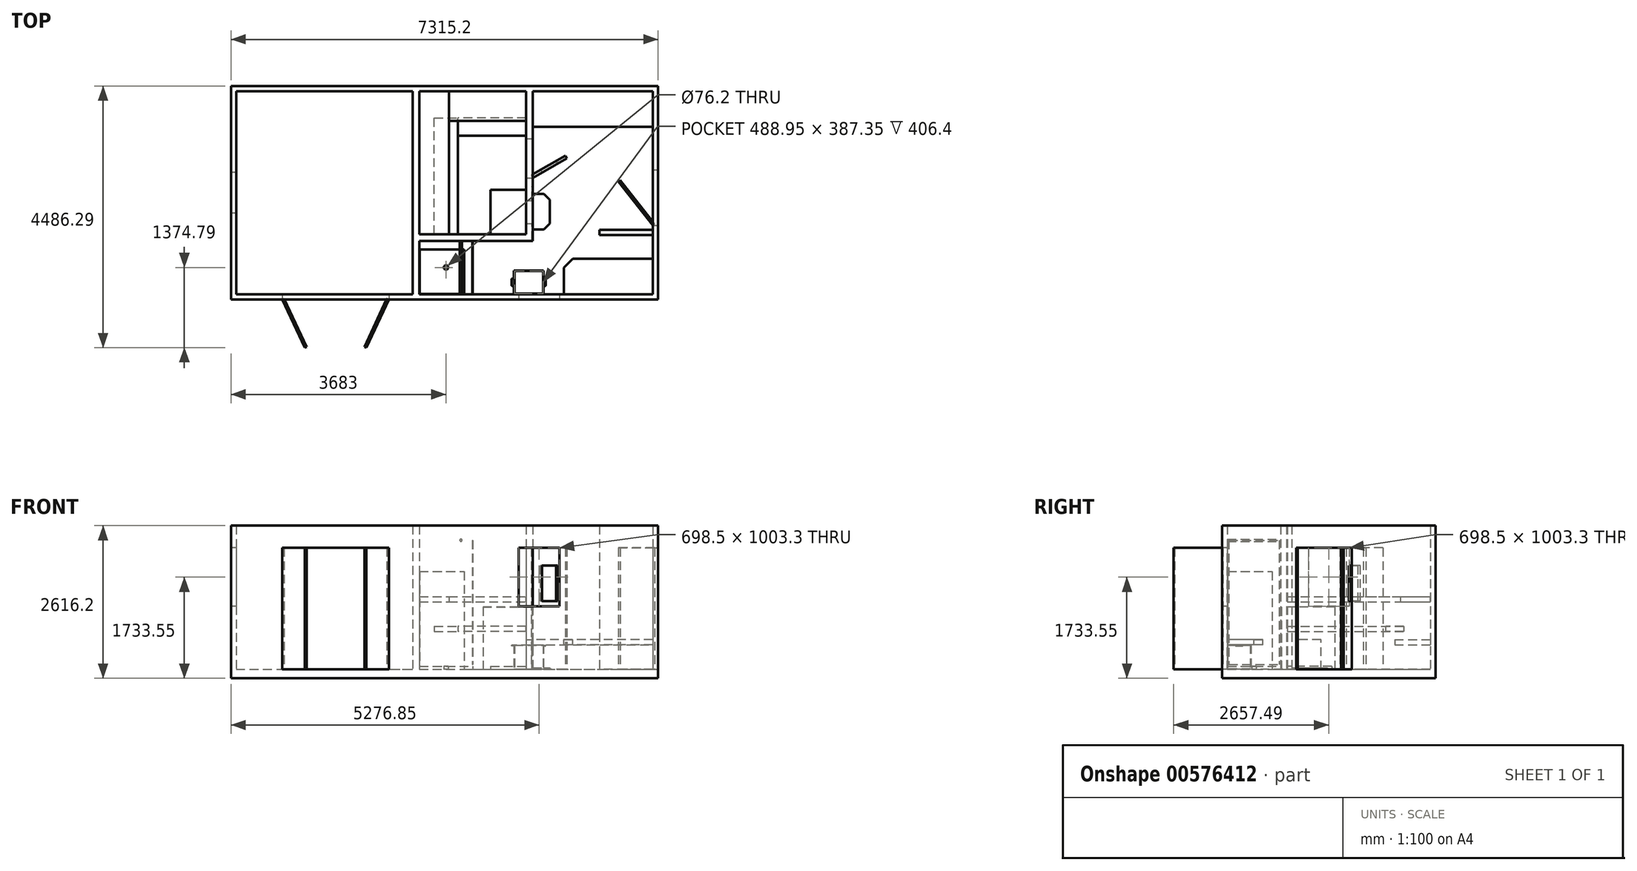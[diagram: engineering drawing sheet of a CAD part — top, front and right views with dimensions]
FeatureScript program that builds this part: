
annotation { "Feature Type Name" : "Feature", "Feature Type Description" : "" }
export const myFeature = defineFeature(function(context is Context, id is Id, definition is map)
    precondition{}
    {
        {
            var Q0;
            Q0=qCreatedBy(makeId("Top.planeOp"),FACE);
            var sketch = newSketch(context, id + "F0", { "sketchPlane" : qUnion([Q0])});
            skLineSegment(sketch, "E0.bottom", {"start": v(-3657.6, -1828.8) * mm, "end": v(3657.6, -1828.8) * mm});
            skLineSegment(sketch, "E0.top", {"start": v(-3657.6, 1828.8) * mm, "end": v(3657.6, 1828.8) * mm});
            skLineSegment(sketch, "E0.left", {"start": v(-3657.6, -1828.8) * mm, "end": v(-3657.6, 1828.8) * mm});
            skLineSegment(sketch, "E0.right", {"start": v(3657.6, -1828.8) * mm, "end": v(3657.6, 1828.8) * mm});
            skPoint(sketch, "E0.middle", {"position": v(0, 0) * mm});
            skSolve(sketch);
        }
        {
            var Q0;
            Q0=makeQuery(id+"F0.imprint","IMPRINT",FACE,{"disambiguationData":[TD([[makeQuery(id+"F0.imprint","IMPRINT",EDGE,{"derivedFrom":sQuery(id+"F0.wireOp",EDGE,"E0.bottom")}),1.0]])]});
            extrude(context, id + "F1", {"entities" : qUnion([Q0]), "depth" : 152.4 * mm});
        }
        {
            var Q0;
            Q0=makeQuery(id+"F1.opExtrude","CAP_FACE",FACE,{"disambiguationData":[OSD([sQuery(id+"F0.wireOp",EDGE,"E0.bottom"),sQuery(id+"F0.wireOp",EDGE,"E0.top"),sQuery(id+"F0.wireOp",EDGE,"E0.left"),sQuery(id+"F0.wireOp",EDGE,"E0.right")])],"isStart":false});
            var sketch = newSketch(context, id + "F2", { "sketchPlane" : qUnion([Q0])});
            skLineSegment(sketch, "E1.0", {"start": v(-3657.6, -1828.8) * mm, "end": v(-3657.6, 1828.8) * mm});
            skLineSegment(sketch, "E1.1", {"start": v(-3657.6, 1828.8) * mm, "end": v(3657.6, 1828.8) * mm});
            skLineSegment(sketch, "E1.2", {"start": v(3657.6, -1828.8) * mm, "end": v(3657.6, 1828.8) * mm});
            skLineSegment(sketch, "E1.3", {"start": v(-3657.6, -1828.8) * mm, "end": v(3657.6, -1828.8) * mm});
            skLineSegment(sketch, "E2.bottom", {"start": v(-3568.7, 1739.9) * mm, "end": v(3568.7, 1739.9) * mm});
            skLineSegment(sketch, "E2.top", {"start": v(-3568.7, -1739.9) * mm, "end": v(3568.7, -1739.9) * mm});
            skLineSegment(sketch, "E2.left", {"start": v(-3568.7, 1739.9) * mm, "end": v(-3568.7, -1739.9) * mm});
            skLineSegment(sketch, "E2.right", {"start": v(3568.7, 1739.9) * mm, "end": v(3568.7, -1739.9) * mm});
            skLineSegment(sketch, "E3", {"start": v(3568.7, 0) * mm, "end": v(0, 0) * mm, "construction": true});
            skSolve(sketch);
        }
        {
            var Q0;
            Q0=qSketchRegion(id+"F2",true);
            extrude(context, id + "F3", {"entities" : qUnion([Q0]), "depth" : 2463.8 * mm});
        }
        {
            var Q0;
            Q0=makeQuery(id+"F3.opExtrude","SWEPT_FACE",FACE,{"disambiguationData":[OSD([sQuery(id+"F2.wireOp",EDGE,"E1.2")])]});
            var sketch = newSketch(context, id + "F4", { "sketchPlane" : qUnion([Q0])});
            skLineSegment(sketch, "E4.bottom", {"start": v(-558.8, 152.4) * mm, "end": v(393.7, 152.4) * mm});
            skLineSegment(sketch, "E4.top", {"start": v(-558.8, 2235.2) * mm, "end": v(393.7, 2235.2) * mm});
            skLineSegment(sketch, "E4.left", {"start": v(-558.8, 152.4) * mm, "end": v(-558.8, 2235.2) * mm});
            skLineSegment(sketch, "E4.right", {"start": v(393.7, 152.4) * mm, "end": v(393.7, 2235.2) * mm});
            skSolve(sketch);
        }
        {
            var Q0;
            Q0=qSketchRegion(id+"F4",true);
            extrude(context, id + "F5", {"entities" : qUnion([Q0]), "operationType" : NewBodyOperationType.REMOVE, "endBound" : BoundingType.UP_TO_NEXT, "oppositeDirection" : true, "depth" : 25.4 * mm});
        }
        {
            var Q0;
            Q0=makeQuery(id+"F3.opExtrude","SWEPT_FACE",FACE,{"disambiguationData":[OSD([sQuery(id+"F2.wireOp",EDGE,"E1.3")])]});
            var sketch = newSketch(context, id + "F6", { "sketchPlane" : qUnion([Q0])});
            skLineSegment(sketch, "E5.bottom", {"start": v(-2781.3, 152.4) * mm, "end": v(-952.5, 152.4) * mm});
            skLineSegment(sketch, "E5.top", {"start": v(-2781.3, 2235.2) * mm, "end": v(-952.5, 2235.2) * mm});
            skLineSegment(sketch, "E5.left", {"start": v(-2781.3, 152.4) * mm, "end": v(-2781.3, 2235.2) * mm});
            skLineSegment(sketch, "E5.right", {"start": v(-952.5, 152.4) * mm, "end": v(-952.5, 2235.2) * mm});
            skLineSegment(sketch, "E6.bottom", {"start": v(1270, 2235.2) * mm, "end": v(1968.5, 2235.2) * mm});
            skLineSegment(sketch, "E6.top", {"start": v(1270, 1231.9) * mm, "end": v(1968.5, 1231.9) * mm});
            skLineSegment(sketch, "E6.left", {"start": v(1270, 2235.2) * mm, "end": v(1270, 1231.9) * mm});
            skLineSegment(sketch, "E6.right", {"start": v(1968.5, 2235.2) * mm, "end": v(1968.5, 1231.9) * mm});
            skSolve(sketch);
        }
        {
            var Q0;
            Q0=qSketchRegion(id+"F6",true);
            extrude(context, id + "F7", {"entities" : qUnion([Q0]), "operationType" : NewBodyOperationType.REMOVE, "endBound" : BoundingType.UP_TO_NEXT, "oppositeDirection" : true, "depth" : 25.4 * mm});
        }
        {
            var Q0;
            Q0=makeQuery(id+"F3.opExtrude","SWEPT_FACE",FACE,{"disambiguationData":[OSD([sQuery(id+"F2.wireOp",EDGE,"E1.0")])]});
            var sketch = newSketch(context, id + "F8", { "sketchPlane" : qUnion([Q0])});
            skLineSegment(sketch, "E7.bottom", {"start": v(-349.25, 2235.2) * mm, "end": v(349.25, 2235.2) * mm});
            skLineSegment(sketch, "E7.top", {"start": v(-349.25, 1231.9) * mm, "end": v(349.25, 1231.9) * mm});
            skLineSegment(sketch, "E7.left", {"start": v(-349.25, 2235.2) * mm, "end": v(-349.25, 1231.9) * mm});
            skLineSegment(sketch, "E7.right", {"start": v(349.25, 2235.2) * mm, "end": v(349.25, 1231.9) * mm});
            skLineSegment(sketch, "E8", {"start": v(0, 2235.2) * mm, "end": v(0, 1231.9) * mm, "construction": true});
            skSolve(sketch);
        }
        {
            var Q0;
            Q0=qSketchRegion(id+"F8",true);
            extrude(context, id + "F9", {"entities" : qUnion([Q0]), "operationType" : NewBodyOperationType.REMOVE, "endBound" : BoundingType.UP_TO_NEXT, "oppositeDirection" : true, "depth" : 25.4 * mm});
        }
        {
            var Q0;
            Q0=makeQuery(id+"F1.opExtrude","CAP_FACE",FACE,{"disambiguationData":[OSD([sQuery(id+"F0.wireOp",EDGE,"E0.bottom"),sQuery(id+"F0.wireOp",EDGE,"E0.top"),sQuery(id+"F0.wireOp",EDGE,"E0.left"),sQuery(id+"F0.wireOp",EDGE,"E0.right")])],"isStart":false});
            var sketch = newSketch(context, id + "F10", { "sketchPlane" : qUnion([Q0])});
            skLineSegment(sketch, "E9.bottom", {"start": v(-546.1, -1739.9) * mm, "end": v(-431.8, -1739.9) * mm});
            skLineSegment(sketch, "E9.top", {"start": v(-546.1, 1739.9) * mm, "end": v(-431.8, 1739.9) * mm});
            skLineSegment(sketch, "E9.left", {"start": v(-546.1, -1739.9) * mm, "end": v(-546.1, 1739.9) * mm});
            skLineSegment(sketch, "E9.right", {"start": v(-431.8, -1739.9) * mm, "end": v(-431.8, 1739.9) * mm});
            skLineSegment(sketch, "E10.top", {"start": v(1397, 1739.9) * mm, "end": v(1511.3, 1739.9) * mm});
            skLineSegment(sketch, "E11", {"start": v(1397, 1739.9) * mm, "end": v(1397, -711.2) * mm});
            skLineSegment(sketch, "E12", {"start": v(1397, -711.2) * mm, "end": v(-431.8, -711.2) * mm});
            skLineSegment(sketch, "E13", {"start": v(-431.8, -711.2) * mm, "end": v(-431.8, -825.5) * mm});
            skLineSegment(sketch, "E14", {"start": v(-431.8, -825.5) * mm, "end": v(1511.3, -825.5) * mm});
            skLineSegment(sketch, "E15", {"start": v(1511.3, -825.5) * mm, "end": v(1511.3, 1739.9) * mm});
            skSolve(sketch);
        }
        {
            var Q0;
            Q0=qSketchRegion(id+"F10",true);
            var Q1;
            Q1=makeQuery(id+"F3.opExtrude","CAP_FACE",FACE,{"disambiguationData":[OSD([sQuery(id+"F2.wireOp",EDGE,"E1.0"),sQuery(id+"F2.wireOp",EDGE,"E1.1"),sQuery(id+"F2.wireOp",EDGE,"E1.2"),sQuery(id+"F2.wireOp",EDGE,"E1.3"),sQuery(id+"F2.wireOp",EDGE,"E2.bottom"),sQuery(id+"F2.wireOp",EDGE,"E2.top"),sQuery(id+"F2.wireOp",EDGE,"E2.left"),sQuery(id+"F2.wireOp",EDGE,"E2.right")])],"isStart":false});
            extrude(context, id + "F11", {"entities" : qUnion([Q0]), "endBound" : BoundingType.UP_TO_SURFACE, "endBoundEntityFace" : qUnion([Q1]), "depth" : 25.4 * mm});
        }
        {
            var Q0;
            Q0=makeQuery(id+"F1.opExtrude","CAP_FACE",FACE,{"disambiguationData":[OSD([sQuery(id+"F0.wireOp",EDGE,"E0.bottom"),sQuery(id+"F0.wireOp",EDGE,"E0.top"),sQuery(id+"F0.wireOp",EDGE,"E0.left"),sQuery(id+"F0.wireOp",EDGE,"E0.right")])],"isStart":false});
            var sketch = newSketch(context, id + "F12", { "sketchPlane" : qUnion([Q0])});
            skLineSegment(sketch, "E16.bottom", {"start": v(3568.7, -723.9) * mm, "end": v(2654.3, -723.9) * mm});
            skLineSegment(sketch, "E16.top", {"start": v(3568.7, -635) * mm, "end": v(2654.3, -635) * mm});
            skLineSegment(sketch, "E16.left", {"start": v(3568.7, -723.9) * mm, "end": v(3568.7, -635) * mm});
            skLineSegment(sketch, "E16.right", {"start": v(2654.3, -723.9) * mm, "end": v(2654.3, -635) * mm});
            skSolve(sketch);
        }
        {
            var Q0;
            Q0=qSketchRegion(id+"F12",true);
            var Q1;
            Q1=makeQuery(id+"F3.opExtrude","CAP_FACE",FACE,{"disambiguationData":[OSD([sQuery(id+"F2.wireOp",EDGE,"E1.0"),sQuery(id+"F2.wireOp",EDGE,"E1.1"),sQuery(id+"F2.wireOp",EDGE,"E1.2"),sQuery(id+"F2.wireOp",EDGE,"E1.3"),sQuery(id+"F2.wireOp",EDGE,"E2.bottom"),sQuery(id+"F2.wireOp",EDGE,"E2.top"),sQuery(id+"F2.wireOp",EDGE,"E2.left"),sQuery(id+"F2.wireOp",EDGE,"E2.right")])],"isStart":false});
            extrude(context, id + "F13", {"entities" : qUnion([Q0]), "endBound" : BoundingType.UP_TO_SURFACE, "endBoundEntityFace" : qUnion([Q1]), "depth" : 25.4 * mm});
        }
        {
            var Q0;
            Q0=makeQuery(id+"F11.opExtrude","SWEPT_FACE",FACE,{"disambiguationData":[OSD([sQuery(id+"F10.wireOp",EDGE,"E15")])]});
            var sketch = newSketch(context, id + "F14", { "sketchPlane" : qUnion([Q0])});
            skLineSegment(sketch, "E17.bottom", {"start": v(254, 152.4) * mm, "end": v(927.1, 152.4) * mm});
            skLineSegment(sketch, "E17.top", {"start": v(254, 2235.2) * mm, "end": v(927.1, 2235.2) * mm});
            skLineSegment(sketch, "E17.left", {"start": v(254, 152.4) * mm, "end": v(254, 2235.2) * mm});
            skLineSegment(sketch, "E17.right", {"start": v(927.1, 152.4) * mm, "end": v(927.1, 2235.2) * mm});
            skSolve(sketch);
        }
        {
            var Q0;
            Q0=qSketchRegion(id+"F14",true);
            extrude(context, id + "F15", {"entities" : qUnion([Q0]), "operationType" : NewBodyOperationType.REMOVE, "endBound" : BoundingType.UP_TO_NEXT, "oppositeDirection" : true, "depth" : 25.4 * mm});
        }
        {
            var Q0;
            Q0=qCreatedBy(makeId("Front.planeOp"),FACE);
            var sketch = newSketch(context, id + "F16", { "sketchPlane" : qUnion([Q0])});
            skLineSegment(sketch, "E18.bottom", {"start": v(-431.8, 152.4) * mm, "end": v(-393.7, 152.4) * mm});
            skLineSegment(sketch, "E18.top", {"start": v(-431.8, 1397) * mm, "end": v(-393.7, 1397) * mm});
            skLineSegment(sketch, "E18.left", {"start": v(-431.8, 152.4) * mm, "end": v(-431.8, 1397) * mm});
            skLineSegment(sketch, "E18.right", {"start": v(-393.7, 152.4) * mm, "end": v(-393.7, 1397) * mm});
            skSolve(sketch);
        }
        {
            var Q0;
            Q0=qSketchRegion(id+"F16",true);
            extrude(context, id + "F17", {"entities" : qUnion([Q0]), "depth" : 88.9 * mm, "symmetric" : true});
        }
        {
            var Q0;
            Q0=makeQuery(id+"F17.opExtrude","SWEPT_BODY",BODY,{"disambiguationData":[OSD([sQuery(id+"F16.wireOp",EDGE,"E18.bottom"),sQuery(id+"F16.wireOp",EDGE,"E18.top"),sQuery(id+"F16.wireOp",EDGE,"E18.left"),sQuery(id+"F16.wireOp",EDGE,"E18.right")])]});
            deleteBodies(context, id + "F18", {"entities" : qUnion([Q0])});
        }
        {
            var Q0;
            Q0=qCreatedBy(makeId("Front.planeOp"),FACE);
            var sketch = newSketch(context, id + "F19", { "sketchPlane" : qUnion([Q0])});
            skLineSegment(sketch, "E19.bottom", {"start": v(-431.8, 1397) * mm, "end": v(76.2, 1397) * mm});
            skLineSegment(sketch, "E19.top", {"start": v(-431.8, 1308.1) * mm, "end": v(76.2, 1308.1) * mm});
            skLineSegment(sketch, "E19.left", {"start": v(-431.8, 1397) * mm, "end": v(-431.8, 1308.1) * mm});
            skLineSegment(sketch, "E19.right", {"start": v(76.2, 1397) * mm, "end": v(76.2, 1308.1) * mm});
            skSolve(sketch);
        }
        {
            var Q0;
            Q0=qSketchRegion(id+"F19",true);
            extrude(context, id + "F20", {"entities" : qUnion([Q0]), "endBound" : BoundingType.UP_TO_NEXT, "depth" : 812.8 * mm, "hasSecondDirection" : true, "secondDirectionBound" : BoundingType.UP_TO_NEXT, "secondDirectionOppositeDirection" : true, "secondDirectionDepth" : 25.4 * mm, "offsetDistance" : 25.4 * mm});
        }
        {
            var Q0;
            Q0=makeQuery(id+"F20.opExtrude","SWEPT_FACE",FACE,{"disambiguationData":[OSD([sQuery(id+"F19.wireOp",EDGE,"E19.bottom")])]});
            var sketch = newSketch(context, id + "F21", { "sketchPlane" : qUnion([Q0])});
            skLineSegment(sketch, "E20.top", {"start": v(76.2, 1231.9) * mm, "end": v(1397, 1231.9) * mm});
            skLineSegment(sketch, "E20.left", {"start": v(76.2, 1231.9) * mm, "end": v(76.2, 1739.9) * mm});
            skLineSegment(sketch, "E20.right", {"start": v(1397, 1231.9) * mm, "end": v(1397, 1739.9) * mm});
            skLineSegment(sketch, "E21", {"start": v(1397, 1739.9) * mm, "end": v(76.2, 1739.9) * mm});
            skSolve(sketch);
        }
        {
            var Q0;
            Q0=qSketchRegion(id+"F21",true);
            var Q1;
            Q1=makeQuery(id+"F20.opExtrude","CAP_VERTEX",VERTEX,{"disambiguationData":[OSD([sQuery(id+"F2.wireOp",EDGE,"E2.top"),sQuery(id+"F19.wireOp",EDGE,"E19.top"),sQuery(id+"F19.wireOp",EDGE,"E19.right")])],"isStart":false});
            extrude(context, id + "F22", {"entities" : qUnion([Q0]), "endBound" : BoundingType.UP_TO_VERTEX, "oppositeDirection" : true, "endBoundEntityVertex" : qUnion([Q1]), "depth" : 25.4 * mm});
        }
        {
            var Q0;
            Q0=qCreatedBy(makeId("Front.planeOp"),FACE);
            var sketch = newSketch(context, id + "F23", { "sketchPlane" : qUnion([Q0])});
            skLineSegment(sketch, "E22.bottom", {"start": v(-177.8, 889) * mm, "end": v(228.6, 889) * mm});
            skLineSegment(sketch, "E22.top", {"start": v(-177.8, 800.1) * mm, "end": v(228.6, 800.1) * mm});
            skLineSegment(sketch, "E22.left", {"start": v(-177.8, 889) * mm, "end": v(-177.8, 800.1) * mm});
            skLineSegment(sketch, "E22.right", {"start": v(228.6, 889) * mm, "end": v(228.6, 800.1) * mm});
            skSolve(sketch);
        }
        {
            var Q0;
            Q0=qSketchRegion(id+"F23",true);
            extrude(context, id + "F24", {"entities" : qUnion([Q0]), "endBound" : BoundingType.UP_TO_NEXT, "depth" : 812.8 * mm, "hasSecondDirection" : true, "secondDirectionOppositeDirection" : true, "secondDirectionDepth" : 1282.7 * mm, "offsetDistance" : 25.4 * mm});
        }
        {
            var Q0;
            Q0=makeQuery(id+"F24.opExtrude","SWEPT_FACE",FACE,{"disambiguationData":[OSD([sQuery(id+"F23.wireOp",EDGE,"E22.bottom")])]});
            var sketch = newSketch(context, id + "F25", { "sketchPlane" : qUnion([Q0])});
            skLineSegment(sketch, "E23.bottom", {"start": v(1397, 1282.7) * mm, "end": v(228.6, 1282.7) * mm});
            skLineSegment(sketch, "E23.top", {"start": v(228.6, 977.9) * mm, "end": v(1397, 977.9) * mm});
            skLineSegment(sketch, "E23.left", {"start": v(228.6, 1282.7) * mm, "end": v(228.6, 977.9) * mm});
            skLineSegment(sketch, "E23.right", {"start": v(1397, 1282.7) * mm, "end": v(1397, 977.9) * mm});
            skSolve(sketch);
        }
        {
            var Q0;
            Q0=makeQuery(id+"F3.opExtrude","SWEPT_FACE",FACE,{"disambiguationData":[OSD([sQuery(id+"F2.wireOp",EDGE,"E2.bottom")])]});
            var sketch = newSketch(context, id + "F26", { "sketchPlane" : qUnion([Q0])});
            skLineSegment(sketch, "E24.bottom", {"start": v(3568.7, 660.4) * mm, "end": v(1511.3, 660.4) * mm});
            skLineSegment(sketch, "E24.top", {"start": v(1511.3, 571.5) * mm, "end": v(3568.7, 571.5) * mm});
            skLineSegment(sketch, "E24.left", {"start": v(3568.7, 660.4) * mm, "end": v(3568.7, 571.5) * mm});
            skLineSegment(sketch, "E24.right", {"start": v(1511.3, 660.4) * mm, "end": v(1511.3, 571.5) * mm});
            skSolve(sketch);
        }
        {
            var Q0;
            Q0=qSketchRegion(id+"F26",true);
            extrude(context, id + "F27", {"entities" : qUnion([Q0]), "depth" : 609.6 * mm});
        }
        {
            var Q0;
            Q0=makeQuery(id+"F27.opExtrude","SWEPT_FACE",FACE,{"disambiguationData":[OSD([sQuery(id+"F26.wireOp",EDGE,"E24.bottom")])]});
            var sketch = newSketch(context, id + "F28", { "sketchPlane" : qUnion([Q0])});
            skLineSegment(sketch, "E25.bottom", {"start": v(1511.3, 1130.3) * mm, "end": v(1917.7, 1130.3) * mm});
            skLineSegment(sketch, "E25.top", {"start": v(1511.3, 114.3) * mm, "end": v(1917.7, 114.3) * mm});
            skLineSegment(sketch, "E25.left", {"start": v(1511.3, 114.3) * mm, "end": v(1511.3, 1130.3) * mm});
            skLineSegment(sketch, "E25.right", {"start": v(1917.7, 114.3) * mm, "end": v(1917.7, 1130.3) * mm});
            skSolve(sketch);
        }
        {
            var Q0;
            Q0=qSketchRegion(id+"F25",true);
            var Q1;
            Q1=makeQuery(id+"F24.opExtrude","CAP_VERTEX",VERTEX,{"disambiguationData":[OSD([sQuery(id+"F23.wireOp",EDGE,"E22.top"),sQuery(id+"F23.wireOp",EDGE,"E22.right")])],"isStart":true});
            extrude(context, id + "F29", {"entities" : qUnion([Q0]), "endBound" : BoundingType.UP_TO_VERTEX, "oppositeDirection" : true, "endBoundEntityVertex" : qUnion([Q1]), "depth" : 25.4 * mm});
        }
        {
            var Q0;
            Q0=makeQuery(id+"F1.opExtrude","CAP_FACE",FACE,{"disambiguationData":[OSD([sQuery(id+"F0.wireOp",EDGE,"E0.bottom"),sQuery(id+"F0.wireOp",EDGE,"E0.top"),sQuery(id+"F0.wireOp",EDGE,"E0.left"),sQuery(id+"F0.wireOp",EDGE,"E0.right")])],"isStart":false});
            var sketch = newSketch(context, id + "F30", { "sketchPlane" : qUnion([Q0])});
            skLineSegment(sketch, "E26", {"start": v(1485.9, 298) * mm, "end": v(1511.3, 254) * mm});
            skLineSegment(sketch, "E27", {"start": v(1511.3, 254) * mm, "end": v(2094.22, 590.55) * mm});
            skLineSegment(sketch, "E28", {"start": v(2094.22, 590.55) * mm, "end": v(2068.82, 634.54) * mm});
            skLineSegment(sketch, "E29", {"start": v(2068.82, 634.54) * mm, "end": v(1485.9, 298) * mm});
            skSolve(sketch);
        }
        {
            var Q0;
            Q0=qSketchRegion(id+"F30",true);
            extrude(context, id + "F31", {"entities" : qUnion([Q0]), "depth" : 2082.8 * mm});
        }
        {
            var Q0;
            Q0=makeQuery(id+"F1.opExtrude","CAP_FACE",FACE,{"disambiguationData":[OSD([sQuery(id+"F0.wireOp",EDGE,"E0.bottom"),sQuery(id+"F0.wireOp",EDGE,"E0.top"),sQuery(id+"F0.wireOp",EDGE,"E0.left"),sQuery(id+"F0.wireOp",EDGE,"E0.right")])],"isStart":false});
            var sketch = newSketch(context, id + "F32", { "sketchPlane" : qUnion([Q0])});
            skLineSegment(sketch, "E30", {"start": v(3568.7, -558.8) * mm, "end": v(3598.59, -535.17) * mm});
            skLineSegment(sketch, "E31", {"start": v(3598.59, -535.17) * mm, "end": v(3007.81, 211.99) * mm});
            skLineSegment(sketch, "E32", {"start": v(3007.81, 211.99) * mm, "end": v(2977.93, 188.36) * mm});
            skLineSegment(sketch, "E33", {"start": v(2977.93, 188.36) * mm, "end": v(3568.7, -558.8) * mm});
            skSolve(sketch);
        }
        {
            var Q0;
            Q0=qSketchRegion(id+"F32",true);
            extrude(context, id + "F33", {"entities" : qUnion([Q0]), "depth" : 2082.8 * mm});
        }
        {
            var Q0;
            Q0=makeQuery(id+"F1.opExtrude","CAP_FACE",FACE,{"disambiguationData":[OSD([sQuery(id+"F0.wireOp",EDGE,"E0.bottom"),sQuery(id+"F0.wireOp",EDGE,"E0.top"),sQuery(id+"F0.wireOp",EDGE,"E0.left"),sQuery(id+"F0.wireOp",EDGE,"E0.right")])],"isStart":false});
            var sketch = newSketch(context, id + "F34", { "sketchPlane" : qUnion([Q0])});
            skLineSegment(sketch, "E34", {"start": v(-431.8, -1739.9) * mm, "end": v(-431.8, -971.55) * mm});
            skLineSegment(sketch, "E35", {"start": v(-431.8, -1739.9) * mm, "end": v(336.55, -1739.9) * mm});
            skLineSegment(sketch, "E36.0", {"start": v(-425.45, -1733.55) * mm, "end": v(336.55, -1733.55) * mm});
            skLineSegment(sketch, "E36.1", {"start": v(-425.45, -1733.55) * mm, "end": v(-425.45, -971.55) * mm});
            skLineSegment(sketch, "E37", {"start": v(-431.8, -971.55) * mm, "end": v(-425.45, -971.55) * mm});
            skLineSegment(sketch, "E38", {"start": v(336.55, -1739.9) * mm, "end": v(336.55, -1733.55) * mm});
            skSolve(sketch);
        }
        {
            var Q0;
            Q0=qSketchRegion(id+"F34",true);
            extrude(context, id + "F35", {"entities" : qUnion([Q0]), "depth" : 1676.4 * mm});
        }
        {
            var Q0;
            Q0=makeQuery(id+"F1.opExtrude","CAP_FACE",FACE,{"disambiguationData":[OSD([sQuery(id+"F0.wireOp",EDGE,"E0.bottom"),sQuery(id+"F0.wireOp",EDGE,"E0.top"),sQuery(id+"F0.wireOp",EDGE,"E0.left"),sQuery(id+"F0.wireOp",EDGE,"E0.right")])],"isStart":false});
            var sketch = newSketch(context, id + "F36", { "sketchPlane" : qUnion([Q0])});
            skLineSegment(sketch, "E39.bottom", {"start": v(-431.8, -1739.9) * mm, "end": v(336.55, -1739.9) * mm});
            skLineSegment(sketch, "E39.top", {"start": v(-431.8, -971.55) * mm, "end": v(336.55, -971.55) * mm});
            skLineSegment(sketch, "E39.left", {"start": v(-431.8, -1739.9) * mm, "end": v(-431.8, -971.55) * mm});
            skLineSegment(sketch, "E39.right", {"start": v(336.55, -1739.9) * mm, "end": v(336.55, -971.55) * mm});
            skSolve(sketch);
        }
        {
            var Q0;
            Q0=qSketchRegion(id+"F36",true);
            extrude(context, id + "F37", {"entities" : qUnion([Q0]), "operationType" : NewBodyOperationType.ADD, "depth" : 50.8 * mm});
        }
        {
            var Q0;
            Q0=makeQuery(id+"F1.opExtrude","CAP_FACE",FACE,{"disambiguationData":[OSD([sQuery(id+"F0.wireOp",EDGE,"E0.bottom"),sQuery(id+"F0.wireOp",EDGE,"E0.top"),sQuery(id+"F0.wireOp",EDGE,"E0.left"),sQuery(id+"F0.wireOp",EDGE,"E0.right")])],"isStart":false});
            var sketch = newSketch(context, id + "F38", { "sketchPlane" : qUnion([Q0])});
            skLineSegment(sketch, "E40.bottom", {"start": v(-431.8, -1739.9) * mm, "end": v(482.6, -1739.9) * mm});
            skLineSegment(sketch, "E40.top", {"start": v(-431.8, -825.5) * mm, "end": v(482.6, -825.5) * mm});
            skLineSegment(sketch, "E40.left", {"start": v(-431.8, -1739.9) * mm, "end": v(-431.8, -825.5) * mm});
            skLineSegment(sketch, "E40.right", {"start": v(482.6, -1739.9) * mm, "end": v(482.6, -825.5) * mm});
            skCircle(sketch, "E41", {"center": v(25.4, -1282.7) * mm, "radius": 38.1 * mm});
            skLineSegment(sketch, "E42", {"start": v(25.4, -825.5) * mm, "end": v(25.4, -1739.9) * mm, "construction": true});
            skSolve(sketch);
        }
        {
            var Q0;
            Q0=qSketchRegion(id+"F38",true);
            extrude(context, id + "F39", {"entities" : qUnion([Q0]), "depth" : 50.8 * mm});
        }
        {
            var Q0;
            Q0=makeQuery(id+"F3.opExtrude","SWEPT_FACE",FACE,{"disambiguationData":[OSD([sQuery(id+"F2.wireOp",EDGE,"E2.top")])]});
            var sketch = newSketch(context, id + "F40", { "sketchPlane" : qUnion([Q0])});
            skLineSegment(sketch, "E43.bottom", {"start": v(-3568.7, 660.4) * mm, "end": v(-2044.7, 660.4) * mm});
            skLineSegment(sketch, "E43.top", {"start": v(-3568.7, 571.5) * mm, "end": v(-2044.7, 571.5) * mm});
            skLineSegment(sketch, "E43.left", {"start": v(-3568.7, 660.4) * mm, "end": v(-3568.7, 571.5) * mm});
            skLineSegment(sketch, "E43.right", {"start": v(-2044.7, 660.4) * mm, "end": v(-2044.7, 571.5) * mm});
            skSolve(sketch);
        }
        {
            var Q0;
            Q0=qSketchRegion(id+"F40",true);
            extrude(context, id + "F41", {"entities" : qUnion([Q0]), "depth" : 609.6 * mm});
        }
        {
            var Q0;
            Q0=makeQuery(id+"F41.opExtrude","SWEPT_FACE",FACE,{"disambiguationData":[OSD([sQuery(id+"F40.wireOp",EDGE,"E43.bottom")])]});
            var sketch = newSketch(context, id + "F42", { "sketchPlane" : qUnion([Q0])});
            skLineSegment(sketch, "E44", {"start": v(2044.7, -1130.3) * mm, "end": v(2044.7, -1282.7) * mm});
            skLineSegment(sketch, "E45", {"start": v(2044.7, -1282.7) * mm, "end": v(2197.1, -1130.3) * mm});
            skLineSegment(sketch, "E46", {"start": v(2197.1, -1130.3) * mm, "end": v(2044.7, -1130.3) * mm});
            skSolve(sketch);
        }
        {
            var Q0;
            Q0=qSketchRegion(id+"F42",true);
            extrude(context, id + "F43", {"entities" : qUnion([Q0]), "operationType" : NewBodyOperationType.REMOVE, "endBound" : BoundingType.UP_TO_NEXT, "oppositeDirection" : true, "depth" : 25.4 * mm});
        }
        {
            var Q0;
            Q0=makeQuery(id+"F31.opExtrude","SWEPT_FACE",FACE,{"disambiguationData":[OSD([sQuery(id+"F30.wireOp",EDGE,"E27")])]});
            var sketch = newSketch(context, id + "F44", { "sketchPlane" : qUnion([Q0])});
            skLineSegment(sketch, "E47.bottom", {"start": v(1619.97, 1930.4) * mm, "end": v(1924.77, 1930.4) * mm});
            skLineSegment(sketch, "E47.top", {"start": v(1619.97, 1320.8) * mm, "end": v(1924.77, 1320.8) * mm});
            skLineSegment(sketch, "E47.left", {"start": v(1619.97, 1930.4) * mm, "end": v(1619.97, 1320.8) * mm});
            skLineSegment(sketch, "E47.right", {"start": v(1924.77, 1930.4) * mm, "end": v(1924.77, 1320.8) * mm});
            skLineSegment(sketch, "E48", {"start": v(1772.37, 2235.2) * mm, "end": v(1772.37, 1930.4) * mm, "construction": true});
            skSolve(sketch);
        }
        {
            var Q0;
            Q0=qSketchRegion(id+"F44",true);
            extrude(context, id + "F45", {"entities" : qUnion([Q0]), "operationType" : NewBodyOperationType.REMOVE, "endBound" : BoundingType.UP_TO_NEXT, "oppositeDirection" : true, "depth" : 25.4 * mm});
        }
        {
            var Q0;
            Q0=makeQuery(id+"F1.opExtrude","CAP_FACE",FACE,{"disambiguationData":[OSD([sQuery(id+"F0.wireOp",EDGE,"E0.bottom"),sQuery(id+"F0.wireOp",EDGE,"E0.top"),sQuery(id+"F0.wireOp",EDGE,"E0.left"),sQuery(id+"F0.wireOp",EDGE,"E0.right")])],"isStart":false});
            var sketch = newSketch(context, id + "F46", { "sketchPlane" : qUnion([Q0])});
            skLineSegment(sketch, "E49", {"start": v(1397, -711.2) * mm, "end": v(787.4, -711.2) * mm});
            skLineSegment(sketch, "E50", {"start": v(787.4, -711.2) * mm, "end": v(787.4, 50.8) * mm});
            skLineSegment(sketch, "E51", {"start": v(787.4, 50.8) * mm, "end": v(1397, 50.8) * mm});
            skLineSegment(sketch, "E52", {"start": v(1397, 50.8) * mm, "end": v(1397, -133.35) * mm});
            skLineSegment(sketch, "E53", {"start": v(1397, -527.05) * mm, "end": v(1498.6, -527.05) * mm});
            skLineSegment(sketch, "E54", {"start": v(1498.6, -527.05) * mm, "end": v(1498.6, -133.35) * mm});
            skLineSegment(sketch, "E55", {"start": v(1498.6, -133.35) * mm, "end": v(1397, -133.35) * mm});
            skLineSegment(sketch, "E56.trimOffspring", {"start": v(1397, -527.05) * mm, "end": v(1397, -711.2) * mm});
            skSolve(sketch);
        }
        {
            var Q0;
            Q0=qSketchRegion(id+"F46",true);
            extrude(context, id + "F47", {"entities" : qUnion([Q0]), "depth" : 50.8 * mm});
        }
        {
            var Q0;
            Q0=makeQuery(id+"F1.opExtrude","CAP_FACE",FACE,{"disambiguationData":[OSD([sQuery(id+"F0.wireOp",EDGE,"E0.bottom"),sQuery(id+"F0.wireOp",EDGE,"E0.top"),sQuery(id+"F0.wireOp",EDGE,"E0.left"),sQuery(id+"F0.wireOp",EDGE,"E0.right")])],"isStart":false});
            var sketch = newSketch(context, id + "F48", { "sketchPlane" : qUnion([Q0])});
            skLineSegment(sketch, "E57", {"start": v(1498.6, -634.57) * mm, "end": v(1701.8, -634.57) * mm});
            skLineSegment(sketch, "E58", {"start": v(1701.8, -634.57) * mm, "end": v(1803.4, -532.97) * mm});
            skLineSegment(sketch, "E59", {"start": v(1803.4, -532.97) * mm, "end": v(1803.4, -126.57) * mm});
            skLineSegment(sketch, "E60", {"start": v(1803.4, -126.57) * mm, "end": v(1701.8, -24.97) * mm});
            skLineSegment(sketch, "E61", {"start": v(1701.8, -24.97) * mm, "end": v(1498.6, -24.97) * mm});
            skLineSegment(sketch, "E62", {"start": v(1498.6, -24.97) * mm, "end": v(1498.6, -634.57) * mm});
            skLineSegment(sketch, "E63", {"start": v(1498.6, -329.77) * mm, "end": v(1803.4, -329.77) * mm, "construction": true});
            skSolve(sketch);
        }
        {
            var Q0;
            Q0=qSketchRegion(id+"F48",true);
            extrude(context, id + "F49", {"entities" : qUnion([Q0]), "depth" : 25.4 * mm});
        }
        {
            var Q0;
            Q0=makeQuery(id+"F11.opExtrude","SWEPT_FACE",FACE,{"disambiguationData":[OSD([sQuery(id+"F10.wireOp",EDGE,"E14")])]});
            var sketch = newSketch(context, id + "F50", { "sketchPlane" : qUnion([Q0])});
            skCircle(sketch, "E64", {"center": v(282.22, 2367.47) * mm, "radius": 19.05 * mm});
            skSolve(sketch);
        }
        {
            var Q0;
            Q0=qSketchRegion(id+"F50",true);
            extrude(context, id + "F51", {"entities" : qUnion([Q0]), "endBound" : BoundingType.UP_TO_NEXT, "depth" : 25.4 * mm, "offsetDistance" : 25.4 * mm});
        }
        {
            var Q0;
            Q0=makeQuery(id+"F39.opExtrude","SWEPT_FACE",FACE,{"disambiguationData":[OSD([sQuery(id+"F38.wireOp",EDGE,"E40.right")])]});
            var sketch = newSketch(context, id + "F52", { "sketchPlane" : qUnion([Q0])});
            skLineSegment(sketch, "E65.bottom", {"start": v(-1714.5, 2363.56) * mm, "end": v(-850.9, 2363.56) * mm});
            skLineSegment(sketch, "E65.top", {"start": v(-1714.5, 238.7) * mm, "end": v(-850.9, 238.7) * mm});
            skLineSegment(sketch, "E65.left", {"start": v(-1714.5, 2363.56) * mm, "end": v(-1714.5, 238.7) * mm});
            skLineSegment(sketch, "E65.right", {"start": v(-850.9, 2363.56) * mm, "end": v(-850.9, 238.7) * mm});
            skSolve(sketch);
        }
        {
            var Q0;
            Q0=qSketchRegion(id+"F52",true);
            extrude(context, id + "F53", {"entities" : qUnion([Q0]), "oppositeDirection" : true, "depth" : 3.17 * mm});
        }
        {
            var Q0;
            Q0=makeQuery(id+"F1.opExtrude","CAP_FACE",FACE,{"disambiguationData":[OSD([sQuery(id+"F0.wireOp",EDGE,"E0.bottom"),sQuery(id+"F0.wireOp",EDGE,"E0.top"),sQuery(id+"F0.wireOp",EDGE,"E0.left"),sQuery(id+"F0.wireOp",EDGE,"E0.right")])],"isStart":false});
            var sketch = newSketch(context, id + "F54", { "sketchPlane" : qUnion([Q0])});
            skLineSegment(sketch, "E66.bottom", {"start": v(1696.48, -1739.9) * mm, "end": v(1188.48, -1739.9) * mm});
            skLineSegment(sketch, "E66.top", {"start": v(1696.48, -1333.5) * mm, "end": v(1188.48, -1333.5) * mm});
            skLineSegment(sketch, "E66.left", {"start": v(1696.48, -1739.9) * mm, "end": v(1696.48, -1333.5) * mm});
            skLineSegment(sketch, "E66.right", {"start": v(1188.48, -1739.9) * mm, "end": v(1188.48, -1333.5) * mm});
            skSolve(sketch);
        }
        {
            var Q0;
            Q0=qSketchRegion(id+"F54",true);
            extrude(context, id + "F55", {"entities" : qUnion([Q0]), "depth" : 9.52 * mm});
        }
        {
            var Q0;
            Q0=makeQuery(id+"F55.opExtrude","CAP_FACE",FACE,{"disambiguationData":[OSD([sQuery(id+"F54.wireOp",EDGE,"E66.bottom"),sQuery(id+"F54.wireOp",EDGE,"E66.top"),sQuery(id+"F54.wireOp",EDGE,"E66.left"),sQuery(id+"F54.wireOp",EDGE,"E66.right")])],"isStart":false});
            var sketch = newSketch(context, id + "F56", { "sketchPlane" : qUnion([Q0])});
            skLineSegment(sketch, "E67", {"start": v(1696.48, -1739.9) * mm, "end": v(1696.48, -1333.5) * mm});
            skLineSegment(sketch, "E68", {"start": v(1696.48, -1333.5) * mm, "end": v(1188.48, -1333.5) * mm});
            skLineSegment(sketch, "E69", {"start": v(1188.48, -1333.5) * mm, "end": v(1188.48, -1739.9) * mm});
            skLineSegment(sketch, "E70", {"start": v(1188.48, -1739.9) * mm, "end": v(1696.48, -1739.9) * mm});
            skLineSegment(sketch, "E71.0", {"start": v(1198, -1730.38) * mm, "end": v(1686.96, -1730.38) * mm});
            skLineSegment(sketch, "E71.1", {"start": v(1198, -1343.03) * mm, "end": v(1198, -1730.38) * mm});
            skLineSegment(sketch, "E71.2", {"start": v(1686.96, -1343.03) * mm, "end": v(1198, -1343.03) * mm});
            skLineSegment(sketch, "E71.3", {"start": v(1686.96, -1730.38) * mm, "end": v(1686.96, -1343.03) * mm});
            skSolve(sketch);
        }
        {
            var Q0;
            Q0=qSketchRegion(id+"F56",true);
            extrude(context, id + "F57", {"entities" : qUnion([Q0]), "operationType" : NewBodyOperationType.ADD, "depth" : 406.4 * mm});
        }
        {
            var Q0;
            Q0=makeQuery(id+"F57.opExtrude","CAP_FACE",FACE,{"disambiguationData":[OSD([sQuery(id+"F56.wireOp",EDGE,"E67"),sQuery(id+"F56.wireOp",EDGE,"E68"),sQuery(id+"F56.wireOp",EDGE,"E69"),sQuery(id+"F56.wireOp",EDGE,"E70"),sQuery(id+"F56.wireOp",EDGE,"E71.0"),sQuery(id+"F56.wireOp",EDGE,"E71.1"),sQuery(id+"F56.wireOp",EDGE,"E71.2"),sQuery(id+"F56.wireOp",EDGE,"E71.3")])],"isStart":false});
            var sketch = newSketch(context, id + "F58", { "sketchPlane" : qUnion([Q0])});
            skLineSegment(sketch, "E72.bottom", {"start": v(1188.48, -1600.2) * mm, "end": v(1163.08, -1600.2) * mm});
            skLineSegment(sketch, "E72.top", {"start": v(1188.48, -1473.2) * mm, "end": v(1163.08, -1473.2) * mm});
            skLineSegment(sketch, "E72.left", {"start": v(1188.48, -1600.2) * mm, "end": v(1188.48, -1473.2) * mm});
            skLineSegment(sketch, "E72.right", {"start": v(1150.38, -1587.5) * mm, "end": v(1150.38, -1485.9) * mm});
            skLineSegment(sketch, "E73.bottom", {"start": v(1696.48, -1600.2) * mm, "end": v(1721.88, -1600.2) * mm});
            skLineSegment(sketch, "E73.top", {"start": v(1696.48, -1473.2) * mm, "end": v(1721.88, -1473.2) * mm});
            skLineSegment(sketch, "E73.left", {"start": v(1696.48, -1600.2) * mm, "end": v(1696.48, -1473.2) * mm});
            skLineSegment(sketch, "E73.right", {"start": v(1734.58, -1587.5) * mm, "end": v(1734.58, -1485.9) * mm});
            skPoint(sketch, "E74.visualSharp", {"position": v(1734.58, -1600.2) * mm});
            skArc(sketch, "E74.filletArc", {"start": v(1721.88, -1600.2) * mm, "mid": v(1730.86, -1596.48) * mm, "end": v(1734.58, -1587.5) * mm});
            skPoint(sketch, "E75.visualSharp", {"position": v(1734.58, -1473.2) * mm});
            skArc(sketch, "E75.filletArc", {"start": v(1734.58, -1485.9) * mm, "mid": v(1730.86, -1476.92) * mm, "end": v(1721.88, -1473.2) * mm});
            skPoint(sketch, "E76.visualSharp", {"position": v(1150.38, -1600.2) * mm});
            skArc(sketch, "E76.filletArc", {"start": v(1150.38, -1587.5) * mm, "mid": v(1154.1, -1596.48) * mm, "end": v(1163.08, -1600.2) * mm});
            skPoint(sketch, "E77.visualSharp", {"position": v(1150.38, -1473.2) * mm});
            skArc(sketch, "E77.filletArc", {"start": v(1163.08, -1473.2) * mm, "mid": v(1154.1, -1476.92) * mm, "end": v(1150.38, -1485.9) * mm});
            skPoint(sketch, "E78", {"position": v(1686.96, -1536.7) * mm});
            skLineSegment(sketch, "E79", {"start": v(1696.48, -1536.7) * mm, "end": v(1188.48, -1536.7) * mm, "construction": true});
            skSolve(sketch);
        }
        {
            var Q0;
            Q0=qSketchRegion(id+"F58",true);
            extrude(context, id + "F59", {"entities" : qUnion([Q0]), "operationType" : NewBodyOperationType.ADD, "oppositeDirection" : true, "depth" : 12.7 * mm});
        }
        {
            var Q0;
            Q0=makeQuery(id+"F1.opExtrude","CAP_FACE",FACE,{"disambiguationData":[OSD([sQuery(id+"F0.wireOp",EDGE,"E0.bottom"),sQuery(id+"F0.wireOp",EDGE,"E0.top"),sQuery(id+"F0.wireOp",EDGE,"E0.left"),sQuery(id+"F0.wireOp",EDGE,"E0.right")])],"isStart":false});
            var sketch = newSketch(context, id + "F60", { "sketchPlane" : qUnion([Q0])});
            skLineSegment(sketch, "E80.bottom", {"start": v(3657.6, -1828.8) * mm, "end": v(3619.5, -1828.8) * mm});
            skLineSegment(sketch, "E80.top", {"start": v(3657.6, 1828.8) * mm, "end": v(3619.5, 1828.8) * mm});
            skLineSegment(sketch, "E80.left", {"start": v(3657.6, -1828.8) * mm, "end": v(3657.6, 1828.8) * mm});
            skLineSegment(sketch, "E80.right", {"start": v(3619.5, -1828.8) * mm, "end": v(3619.5, 1828.8) * mm});
            skLineSegment(sketch, "E81.1.0.0", {"start": v(3213.1, -1828.8) * mm, "end": v(3213.1, 1828.8) * mm});
            skLineSegment(sketch, "E81.1.0.1", {"start": v(3251.2, -1828.8) * mm, "end": v(3251.2, 1828.8) * mm});
            skLineSegment(sketch, "E81.2.0.0", {"start": v(2806.7, -1828.8) * mm, "end": v(2806.7, 1828.8) * mm});
            skLineSegment(sketch, "E81.2.0.1", {"start": v(2844.8, -1828.8) * mm, "end": v(2844.8, 1828.8) * mm});
            skLineSegment(sketch, "E81.3.0.0", {"start": v(2400.3, -1828.8) * mm, "end": v(2400.3, 1828.8) * mm});
            skLineSegment(sketch, "E81.3.0.1", {"start": v(2438.4, -1828.8) * mm, "end": v(2438.4, 1828.8) * mm});
            skLineSegment(sketch, "E81.4.0.0", {"start": v(1993.9, -1828.8) * mm, "end": v(1993.9, 1828.8) * mm});
            skLineSegment(sketch, "E81.4.0.1", {"start": v(2032, -1828.8) * mm, "end": v(2032, 1828.8) * mm});
            skLineSegment(sketch, "E81.5.0.0", {"start": v(1587.5, -1828.8) * mm, "end": v(1587.5, 1828.8) * mm});
            skLineSegment(sketch, "E81.5.0.1", {"start": v(1625.6, -1828.8) * mm, "end": v(1625.6, 1828.8) * mm});
            skLineSegment(sketch, "E81.6.0.0", {"start": v(1181.1, -1828.8) * mm, "end": v(1181.1, 1828.8) * mm});
            skLineSegment(sketch, "E81.6.0.1", {"start": v(1219.2, -1828.8) * mm, "end": v(1219.2, 1828.8) * mm});
            skLineSegment(sketch, "E81.7.0.0", {"start": v(774.7, -1828.8) * mm, "end": v(774.7, 1828.8) * mm});
            skLineSegment(sketch, "E81.7.0.1", {"start": v(812.8, -1828.8) * mm, "end": v(812.8, 1828.8) * mm});
            skLineSegment(sketch, "E81.8.0.0", {"start": v(368.3, -1828.8) * mm, "end": v(368.3, 1828.8) * mm});
            skLineSegment(sketch, "E81.8.0.1", {"start": v(406.4, -1828.8) * mm, "end": v(406.4, 1828.8) * mm});
            skLineSegment(sketch, "E81.9.0.0", {"start": v(-38.1, -1828.8) * mm, "end": v(-38.1, 1828.8) * mm});
            skLineSegment(sketch, "E81.9.0.1", {"start": v(0, -1828.8) * mm, "end": v(0, 1828.8) * mm});
            skLineSegment(sketch, "E81.10.0.0", {"start": v(-444.5, -1828.8) * mm, "end": v(-444.5, 1828.8) * mm});
            skLineSegment(sketch, "E81.10.0.1", {"start": v(-406.4, -1828.8) * mm, "end": v(-406.4, 1828.8) * mm});
            skLineSegment(sketch, "E81.11.0.0", {"start": v(-850.9, -1828.8) * mm, "end": v(-850.9, 1828.8) * mm});
            skLineSegment(sketch, "E81.11.0.1", {"start": v(-812.8, -1828.8) * mm, "end": v(-812.8, 1828.8) * mm});
            skLineSegment(sketch, "E81.12.0.0", {"start": v(-1257.3, -1828.8) * mm, "end": v(-1257.3, 1828.8) * mm});
            skLineSegment(sketch, "E81.12.0.1", {"start": v(-1219.2, -1828.8) * mm, "end": v(-1219.2, 1828.8) * mm});
            skLineSegment(sketch, "E81.13.0.0", {"start": v(-1663.7, -1828.8) * mm, "end": v(-1663.7, 1828.8) * mm});
            skLineSegment(sketch, "E81.13.0.1", {"start": v(-1625.6, -1828.8) * mm, "end": v(-1625.6, 1828.8) * mm});
            skLineSegment(sketch, "E81.14.0.0", {"start": v(-2070.1, -1828.8) * mm, "end": v(-2070.1, 1828.8) * mm});
            skLineSegment(sketch, "E81.14.0.1", {"start": v(-2032, -1828.8) * mm, "end": v(-2032, 1828.8) * mm});
            skLineSegment(sketch, "E81.15.0.0", {"start": v(-2476.5, -1828.8) * mm, "end": v(-2476.5, 1828.8) * mm});
            skLineSegment(sketch, "E81.15.0.1", {"start": v(-2438.4, -1828.8) * mm, "end": v(-2438.4, 1828.8) * mm});
            skLineSegment(sketch, "E81.16.0.0", {"start": v(-2882.9, -1828.8) * mm, "end": v(-2882.9, 1828.8) * mm});
            skLineSegment(sketch, "E81.16.0.1", {"start": v(-2844.8, -1828.8) * mm, "end": v(-2844.8, 1828.8) * mm});
            skLineSegment(sketch, "E81.17.0.0", {"start": v(-3289.3, -1828.8) * mm, "end": v(-3289.3, 1828.8) * mm});
            skLineSegment(sketch, "E81.17.0.1", {"start": v(-3251.2, -1828.8) * mm, "end": v(-3251.2, 1828.8) * mm});
            skLineSegment(sketch, "E81.direction1", {"start": v(3619.5, -1828.8) * mm, "end": v(3213.1, -1828.8) * mm, "construction": true});
            skLineSegment(sketch, "E82.bottom", {"start": v(254, -2336.8) * mm, "end": v(1473.2, -2336.8) * mm});
            skLineSegment(sketch, "E82.top", {"start": v(254, -3352.8) * mm, "end": v(1473.2, -3352.8) * mm});
            skLineSegment(sketch, "E82.left", {"start": v(254, -2336.8) * mm, "end": v(254, -3352.8) * mm});
            skLineSegment(sketch, "E82.right", {"start": v(1473.2, -2336.8) * mm, "end": v(1473.2, -3352.8) * mm});
            skSolve(sketch);
        }
        {
            var Q0;
            Q0=makeQuery(id+"F11.opExtrude","SWEPT_FACE",FACE,{"disambiguationData":[OSD([sQuery(id+"F10.wireOp",EDGE,"E15")])]});
            var sketch = newSketch(context, id + "F61", { "sketchPlane" : qUnion([Q0])});
            skLineSegment(sketch, "E83.bottom", {"start": v(107.95, 152.4) * mm, "end": v(-825.5, 152.4) * mm});
            skLineSegment(sketch, "E83.top", {"start": v(107.95, 1219.2) * mm, "end": v(-825.5, 1219.2) * mm});
            skLineSegment(sketch, "E83.left", {"start": v(107.95, 152.4) * mm, "end": v(107.95, 1219.2) * mm});
            skLineSegment(sketch, "E83.right", {"start": v(-825.5, 152.4) * mm, "end": v(-825.5, 1219.2) * mm});
            skSolve(sketch);
        }
        {
            var Q0;
            Q0 = qSketchRegion(id + "F61", true);
            extrude(context, id + "F62", {"entities" : qUnion([Q0]), "operationType" : NewBodyOperationType.REMOVE, "oppositeDirection" : true, "depth" : 12.7 * mm, "offsetDistance" : 25.4 * mm});
        }
        {
            var Q0;
            Q0=makeQuery(id+"F62.boolean.opBoolean","COPY",FACE,{"derivedFrom":makeQuery(id+"F62.opExtrude","CAP_FACE",FACE,{"disambiguationData":[OSD([sQuery(id+"F61.wireOp",EDGE,"E83.bottom"),sQuery(id+"F61.wireOp",EDGE,"E83.top"),sQuery(id+"F61.wireOp",EDGE,"E83.left"),sQuery(id+"F61.wireOp",EDGE,"E83.right")])],"isStart":false})});
            var sketch = newSketch(context, id + "F63", { "sketchPlane" : qUnion([Q0])});
            skLineSegment(sketch, "E84.bottom", {"start": v(-133.35, 152.4) * mm, "end": v(-527.05, 152.4) * mm});
            skLineSegment(sketch, "E84.top", {"start": v(-133.35, 660.4) * mm, "end": v(-527.05, 660.4) * mm});
            skLineSegment(sketch, "E84.left", {"start": v(-133.35, 152.4) * mm, "end": v(-133.35, 660.4) * mm});
            skLineSegment(sketch, "E84.right", {"start": v(-527.05, 152.4) * mm, "end": v(-527.05, 660.4) * mm});
            skSolve(sketch);
        }
        {
            var Q0;
            Q0 = qSketchRegion(id + "F63", true);
            extrude(context, id + "F64", {"entities" : qUnion([Q0]), "operationType" : NewBodyOperationType.REMOVE, "endBound" : BoundingType.UP_TO_NEXT, "oppositeDirection" : true, "depth" : 25.4 * mm, "offsetDistance" : 25.4 * mm});
        }
        {
            var Q0;
            Q0=makeQuery(id+"F1.opExtrude","CAP_FACE",FACE,{"disambiguationData":[OSD([sQuery(id+"F0.wireOp",EDGE,"E0.bottom"),sQuery(id+"F0.wireOp",EDGE,"E0.top"),sQuery(id+"F0.wireOp",EDGE,"E0.left"),sQuery(id+"F0.wireOp",EDGE,"E0.right")])],"isStart":false});
            var sketch = newSketch(context, id + "F65", { "sketchPlane" : qUnion([Q0])});
            skLineSegment(sketch, "E85", {"start": v(-2781.3, -1828.8) * mm, "end": v(-2746.77, -1812.7) * mm});
            skLineSegment(sketch, "E86", {"start": v(-2746.77, -1812.7) * mm, "end": v(-2360.25, -2641.39) * mm});
            skLineSegment(sketch, "E87", {"start": v(-2360.25, -2641.39) * mm, "end": v(-2394.78, -2657.5) * mm});
            skLineSegment(sketch, "E88", {"start": v(-2394.78, -2657.5) * mm, "end": v(-2781.3, -1828.8) * mm});
            skLineSegment(sketch, "E89", {"start": v(-952.5, -1828.8) * mm, "end": v(-987.03, -1812.7) * mm});
            skLineSegment(sketch, "E90", {"start": v(-987.03, -1812.7) * mm, "end": v(-1373.55, -2641.39) * mm});
            skLineSegment(sketch, "E91", {"start": v(-1373.55, -2641.39) * mm, "end": v(-1339.02, -2657.5) * mm});
            skLineSegment(sketch, "E92", {"start": v(-1339.02, -2657.5) * mm, "end": v(-952.5, -1828.8) * mm});
            skSolve(sketch);
        }
        {
            var Q0;
            Q0 = qSketchRegion(id + "F65", true);
            extrude(context, id + "F66", {"entities" : qUnion([Q0]), "depth" : 2082.8 * mm, "offsetDistance" : 25.4 * mm});
        }
        {
            var Q0;
            Q0=makeQuery(id+"F11.opExtrude","SWEPT_FACE",FACE,{"disambiguationData":[OSD([sQuery(id+"F10.wireOp",EDGE,"E14")])]});
            var sketch = newSketch(context, id + "F67", { "sketchPlane" : qUnion([Q0])});
            skLineSegment(sketch, "E93.bottom", {"start": v(1511.3, 1219.2) * mm, "end": v(660.4, 1219.2) * mm});
            skLineSegment(sketch, "E93.top", {"start": v(1511.3, 152.4) * mm, "end": v(660.4, 152.4) * mm});
            skLineSegment(sketch, "E93.left", {"start": v(1511.3, 1219.2) * mm, "end": v(1511.3, 152.4) * mm});
            skLineSegment(sketch, "E93.right", {"start": v(660.4, 1219.2) * mm, "end": v(660.4, 152.4) * mm});
            skSolve(sketch);
        }
        {
            var Q0;
            Q0 = qSketchRegion(id + "F67", true);
            extrude(context, id + "F68", {"entities" : qUnion([Q0]), "operationType" : NewBodyOperationType.REMOVE, "oppositeDirection" : true, "depth" : 12.7 * mm, "offsetDistance" : 25.4 * mm});
        }
    });
